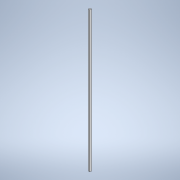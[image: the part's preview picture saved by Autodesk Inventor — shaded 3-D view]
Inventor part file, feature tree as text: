
AUTODESK INVENTOR PART (.ipt)
format: ipt  version: 2022 (Build 260153000, 153)  size: 149,504 bytes
history: native  units: mm
features: extrude x1, sketch x1
ambient origin geometry x8: Origin, YZ Plane, XZ Plane, XY Plane, X Axis, Y Axis, Z Axis, Center Point
bodies: Body1 (feature_tree)
feature tree (2):
  extrude  "Extrusion7"  Depth=5.0mm
  sketch  "Sketch4"  dims[d31=34.456mm d103=5.0mm d104=5.0mm d105=487.0mm d106=0.0mm]
